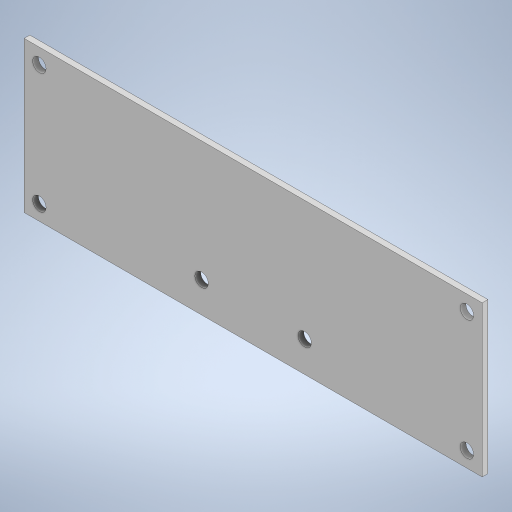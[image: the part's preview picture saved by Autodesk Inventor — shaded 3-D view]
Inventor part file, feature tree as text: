
AUTODESK INVENTOR PART (.ipt)
format: ipt  version: 2023 (Build 270158000, 158)  size: 233,472 bytes
history: native  units: mm
features: extrude x3, sketch x3
ambient origin geometry x8: Origin, YZ Plane, XZ Plane, XY Plane, X Axis, Y Axis, Z Axis, Center Point
bodies: Body1 (feature_tree)
feature tree (6):
  extrude  "Extrusion45"  Depth=79.0mm
  extrude  "Extrusion47"  Depth=3.0mm
  extrude  "Extrusion48"  Depth=7.0mm
  sketch  "Sketch66"  dims[d179=240.0mm d180=79.0mm]
  sketch  "Sketch68"  dims[d181=3.0mm d182=0.0mm d186=7.0mm]
  sketch  "Sketch69"  dims[d187=7.0mm d188=7.0mm d189=7.0mm d190=0.0mm d191=0.0mm d192=7.0mm d193=7.0mm d194=0.0mm d195=0.0mm d49=0.5mm d50=0.872665mm d51=0.5mm d52=0.872665mm d130=0.5mm d131=0.872665mm d132=0.5mm d133=0.872665mm d156=0.5mm d157=0.872665mm d158=0.5mm d159=0.872665mm]
